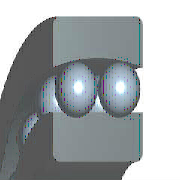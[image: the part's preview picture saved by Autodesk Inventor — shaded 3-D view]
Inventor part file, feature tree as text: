
AUTODESK INVENTOR PART (.ipt)
format: ipt  version: 2022.1 (Build 261234000, 234)  size: 388,608 bytes
history: native  units: mm (DEFAULTED — no unit token found)
features: other x3, sketch x1, pattern_circular x1, pattern_linear x1
ambient origin geometry x8: Origin, YZ Plane, XZ Plane, XY Plane, X Axis, Y Axis, Z Axis, Center Point
bodies: Solid1 (feature_tree)
feature tree (6):
  sketch  "Boceto1"  dims[d19=90.0deg d0=1.0mm d1=180.0deg d2=120.0mm d3=360.0deg d4=6.08mm d5=0.0mm d6=0.0mm d7=0.0mm d8=30.0mm d9=62.0mm d10=16.0mm d11=4.64mm d12=40.432mm d13=46.0mm d14=0.0mm d15=0.0mm d16=180.0deg d17=20.0mm d18=-6.72mm]
  other  "Cuerpo"
  other  "Bola1"
  other  "Bola2"
  pattern_circular  "Bolas1"  [2 undecoded]
  pattern_linear  "Bolas2"  Spacing1=180.0deg  [1 undecoded]
note: 3 required parameter values undecoded (feature->parameter linkage not recoverable at this tier; creation-order binding heuristic only, values carry confidence <= 0.55)
